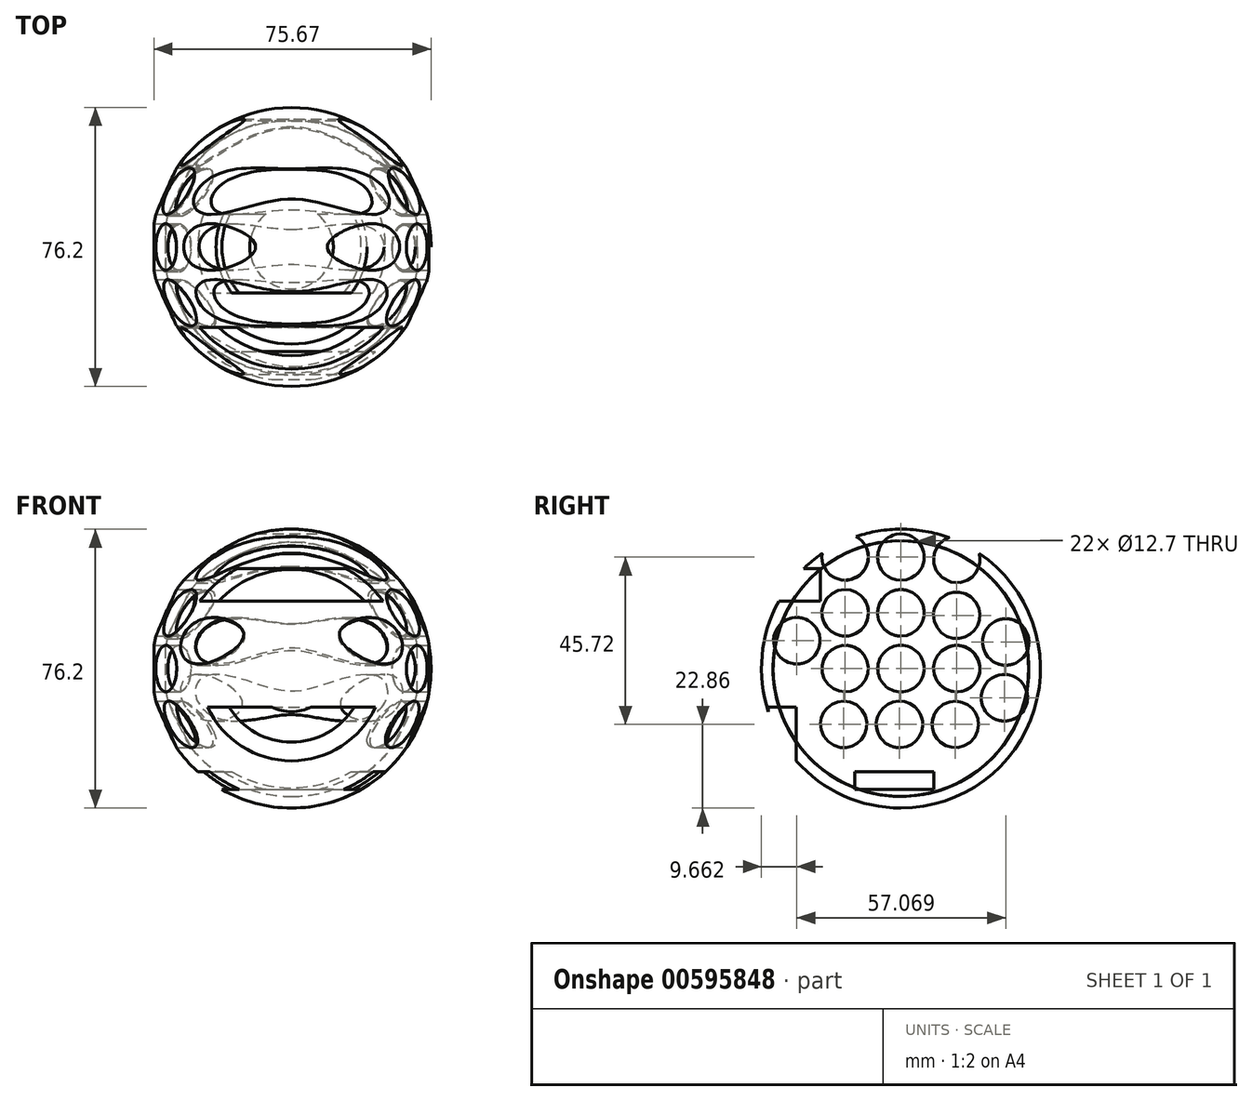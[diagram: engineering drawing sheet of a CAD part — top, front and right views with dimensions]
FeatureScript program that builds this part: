
annotation { "Feature Type Name" : "Feature", "Feature Type Description" : "" }
export const myFeature = defineFeature(function(context is Context, id is Id, definition is map)
    precondition{}
    {
        {
            var Q0;
            Q0=qCreatedBy(makeId("Front.planeOp"),FACE);
            var sketch = newSketch(context, id + "F0", { "sketchPlane" : qUnion([Q0])});
            skArc(sketch, "E0", {"start": v(0, -38.1) * mm, "mid": v(38.1, 0) * mm, "end": v(0, 38.1) * mm});
            skArc(sketch, "E1", {"start": v(0, -34.93) * mm, "mid": v(34.93, 0) * mm, "end": v(0, 34.93) * mm});
            skLineSegment(sketch, "E2", {"start": v(0, 48.84) * mm, "end": v(0, -47.22) * mm, "construction": true});
            skLineSegment(sketch, "E3", {"start": v(0, 38.1) * mm, "end": v(0, 34.93) * mm});
            skLineSegment(sketch, "E4", {"start": v(0, -34.93) * mm, "end": v(0, -38.1) * mm});
            skSolve(sketch);
        }
        {
            var Q0;
            Q0=makeQuery(id+"F0.imprint","IMPRINT",FACE,{"disambiguationData":[TD([[makeQuery(id+"F0.imprint","IMPRINT",EDGE,{"derivedFrom":sQuery(id+"F0.wireOp",EDGE,"E0")}),1.0]])]});
            var Q1;
            Q1=sQuery(id+"F0.wireOp",EDGE,"E2");
            revolve(context, id + "F1", {"entities" : qUnion([Q0]), "axis" : qUnion([Q1]), "revolveType" : RevolveType.FULL});
        }
        {
            var Q0;
            Q0=qCreatedBy(makeId("Right.planeOp"),FACE);
            var sketch = newSketch(context, id + "F2", { "sketchPlane" : qUnion([Q0])});
            skCircle(sketch, "E5", {"center": v(0, 0) * mm, "radius": 6.35 * mm});
            skCircle(sketch, "E6", {"center": v(-15.24, 0) * mm, "radius": 6.35 * mm});
            skCircle(sketch, "E7", {"center": v(0, 15.24) * mm, "radius": 6.35 * mm});
            skCircle(sketch, "E8", {"center": v(0, 30.48) * mm, "radius": 6.35 * mm});
            skCircle(sketch, "E9", {"center": v(15.24, 0) * mm, "radius": 6.35 * mm});
            skCircle(sketch, "E10", {"center": v(15.24, 14.55) * mm, "radius": 6.35 * mm});
            skCircle(sketch, "E11", {"center": v(-15.24, 15.24) * mm, "radius": 6.35 * mm});
            skCircle(sketch, "E12", {"center": v(-0.4, -15.24) * mm, "radius": 6.35 * mm});
            skCircle(sketch, "E13", {"center": v(14.85, -15.24) * mm, "radius": 6.35 * mm});
            skCircle(sketch, "E14", {"center": v(28.24, -7.96) * mm, "radius": 6.35 * mm});
            skCircle(sketch, "E15", {"center": v(28.63, 7.28) * mm, "radius": 6.35 * mm});
            skCircle(sketch, "E16", {"center": v(15.24, 29.8) * mm, "radius": 6.35 * mm});
            skCircle(sketch, "E17", {"center": v(-15.24, 30.48) * mm, "radius": 6.35 * mm});
            skCircle(sketch, "E18", {"center": v(-28.44, 7.62) * mm, "radius": 6.35 * mm});
            skCircle(sketch, "E19", {"center": v(-15.63, -15.23) * mm, "radius": 6.35 * mm});
            skLineSegment(sketch, "E20.bottom", {"start": v(9.03, -28.2) * mm, "end": v(-12.61, -28.2) * mm});
            skLineSegment(sketch, "E20.top", {"start": v(9.03, -33) * mm, "end": v(-12.61, -33) * mm});
            skLineSegment(sketch, "E20.left", {"start": v(9.03, -28.2) * mm, "end": v(9.03, -33) * mm});
            skLineSegment(sketch, "E20.right", {"start": v(-12.61, -28.2) * mm, "end": v(-12.61, -33) * mm});
            skLineSegment(sketch, "E21.bottom", {"start": v(-28.58, -10.48) * mm, "end": v(-36.23, -10.48) * mm});
            skLineSegment(sketch, "E21.top", {"start": v(-28.58, -26.88) * mm, "end": v(-36.23, -26.88) * mm});
            skLineSegment(sketch, "E21.left", {"start": v(-28.58, -10.48) * mm, "end": v(-28.58, -26.88) * mm});
            skLineSegment(sketch, "E21.right", {"start": v(-36.23, -10.48) * mm, "end": v(-36.23, -26.88) * mm});
            skLineSegment(sketch, "E22.bottom", {"start": v(-22.02, 27.35) * mm, "end": v(-39.95, 27.35) * mm});
            skLineSegment(sketch, "E22.top", {"start": v(-22.02, 18.38) * mm, "end": v(-39.95, 18.38) * mm});
            skLineSegment(sketch, "E22.left", {"start": v(-22.02, 27.35) * mm, "end": v(-22.02, 18.38) * mm});
            skLineSegment(sketch, "E22.right", {"start": v(-39.95, 27.35) * mm, "end": v(-39.95, 18.38) * mm});
            skSolve(sketch);
        }
        {
            var Q0;
            Q0 = qSketchRegion(id + "F2", true);
            extrude(context, id + "F3", {"entities" : qUnion([Q0]), "operationType" : NewBodyOperationType.REMOVE, "endBound" : BoundingType.SYMMETRIC, "oppositeDirection" : true, "depth" : 101.6 * mm, "offsetDistance" : 25.4 * mm});
        }
    });
